# Revit family: Andreu World Reverse Conference ME5720
name_source: partatom
category: Mobiliario
revit_build: Autodesk Revit 2014 (Build: 20130722_2115(x64)
units: mm (PartAtom-declared; Revit-internal decimal feet)

## types (1)
- ME-5720 6500x1500 Cement
    Base Material = Andreu World Cement Finish
    Dekton Width = 1440 mm  [stored 4.72441 ft]
    Descripción = Table
    Fabricante = Andreu World
    Height = 715 mm  [stored 2.3458 ft]
    Modelo = Reverse Conference
    P.C. = 2500 mm  [stored 8.2021 ft]
    R Base = 250 mm  [stored 0.82021 ft]
    Reference = ME-5720
    Top = Sí
    Top Base = 715 mm  [stored 2.3458 ft]
    Top Length = 6500 mm  [stored 21.3255 ft]
    Top Material = Andreu World Cement Finish
    Top Thickness = 30 mm  [stored 0.0984252 ft]
    Top Width = 1500 mm  [stored 4.92126 ft]
    URL = http://www.andreuworld.com

note: [stored X ft] marks values corroborated as IEEE doubles in the binary element streams (Revit-internal decimal feet)

## geometry (parser evidence)
native form markers: Blend x8
no freeform markers — native parametric forms only
